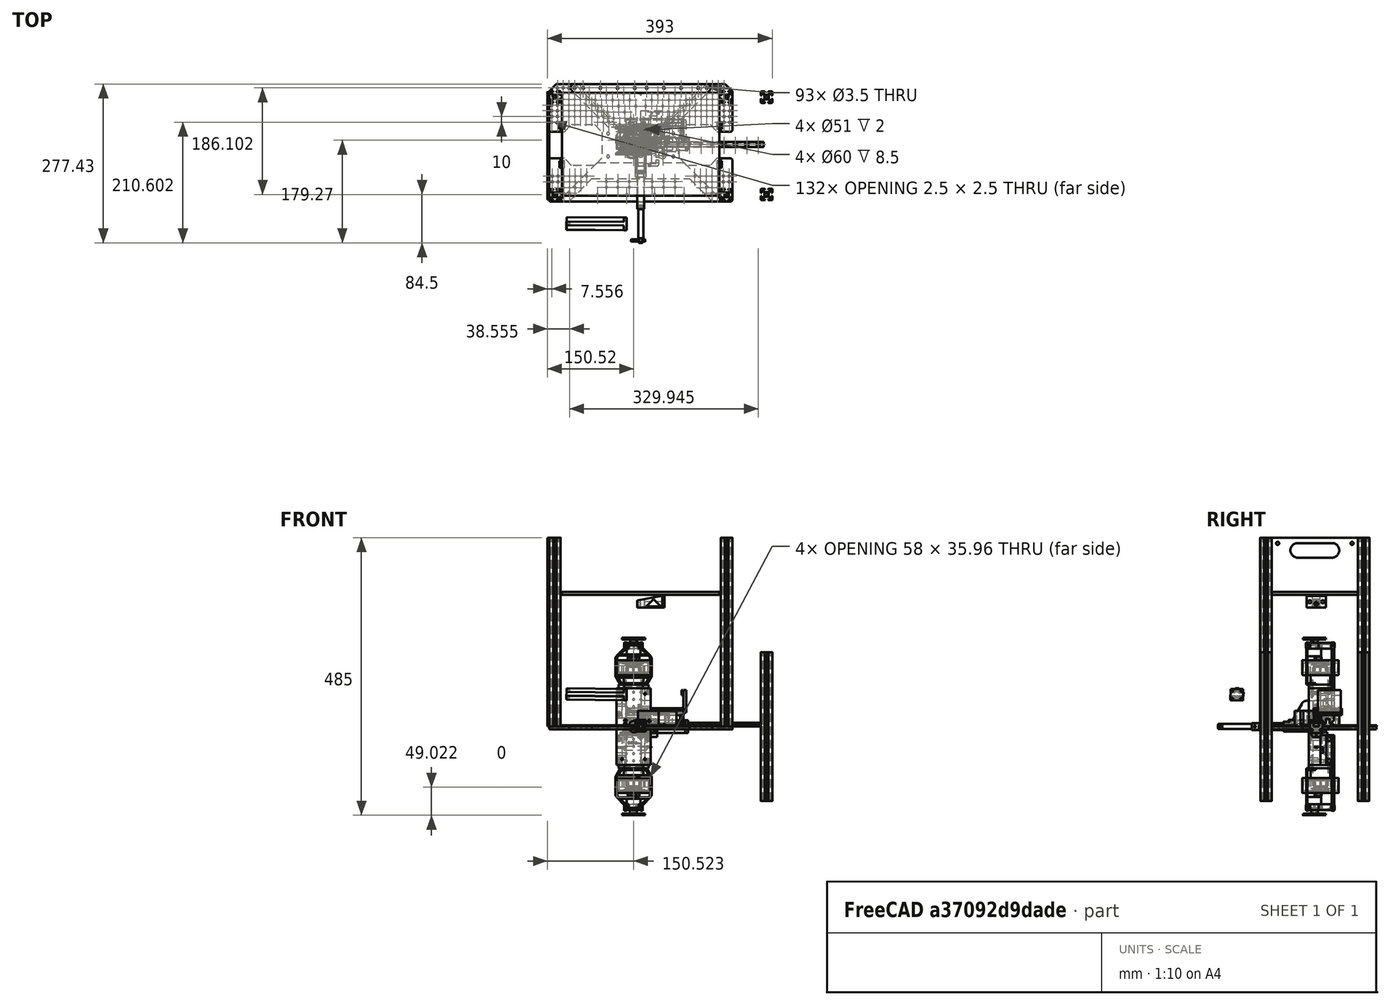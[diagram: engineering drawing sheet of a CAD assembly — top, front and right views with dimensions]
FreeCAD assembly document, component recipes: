
FREECAD ASSEMBLY — COMPONENT RECIPES ("NutSorter")

This assembly document has 31 components, labeled P0..P30 below (a component is one placed body or linked part). 29 of them carry a construction recipe — the FreeCAD feature program that regenerates the part from scratch, quoted from this document or its linked companion documents; the rest are supplied as boundary geometry only. No exploded tour is included for this assembly.
NOTE — document 2 of 2 of this assembly tour. The two overview renders and the header above are repeated from document 1; the component sections below continue where the previous document stopped.
COMPONENT P25 — recipe-attached ("Hiwin MGN9", modeled in this document).
Construction recipe (the document's own serialized feature program — sketch geometry with constraints, then the solid features built on it; lengths are millimeters unless a unit is written):

FEATURE [Sketcher::SketchObject] Sketch031
  ArcFitTolerance = 0
  AttachmentSupport = -> [YZ_Plane013]
  FullyConstrained = true
  MakeInternals = false
  MapMode = 5
  Placement = pos=(0,0,0) rot=(0.57735,0.57735,0.57735;2.0944rad)
  sketch-geometry (4):
    g0: LineSegment StartX=-4.5 StartY=0 StartZ=0 EndX=4.5 EndY=0 EndZ=0
    g1: LineSegment StartX=4.5 StartY=0 StartZ=0 EndX=4.5 EndY=6.5 EndZ=0
    g2: LineSegment StartX=4.5 StartY=6.5 StartZ=0 EndX=-4.5 EndY=6.5 EndZ=0
    g3: LineSegment StartX=-4.5 StartY=6.5 StartZ=0 EndX=-4.5 EndY=0 EndZ=0
  constraints (11):
    c: Coincident(g0,g1)
    c: Coincident(g1,g2)
    c: Coincident(g2,g3)
    c: Coincident(g3,g0)
    c: Horizontal(g0)
    c: Horizontal(g2)
    c: Vertical(g1)
    c: Vertical(g3)
    c: Symmetric(g0,g0,g-1)
    c: DistanceX(g0,g0) = 9  'width'
    c: DistanceY(g1,g1) = 6.5  'height'
FEATURE [PartDesign::Pad] Pad012
  Direction = (1,0,0)
  Length = 215
  Length2 = 10
  Placement = pos=(0,0,0) rot=(0.57735,0.57735,0.57735;2.0944rad)
  Profile = -> Sketch031
  ReferenceAxis = -> Sketch031 [N_Axis]
  Suppressed = false
  Type = 0
  expr: Length = Spreadsheet001.length
FEATURE [Sketcher::SketchObject] Sketch032
  ArcFitTolerance = 0
  AttachmentSupport = -> [YZ_Plane013]
  FullyConstrained = true
  MakeInternals = false
  MapMode = 5
  Placement = pos=(0,0,0) rot=(0.57735,-0.57735,-0.57735;2.0944rad)
  expr: Constraints[13] = 6.5 - 1.8
  expr: Constraints[14] = <<Sketch031>>.Constraints.width / 2 + 0.1 mm
  sketch-geometry (10):
    g0: ArcOfCircle CenterX=-4.6 CenterY=4.7 CenterZ=0 NormalX=0 NormalY=0 NormalZ=1 AngleXU=0 Radius=1 StartAngle=0.25268 EndAngle=6.03051
    g1: LineSegment StartX=-3.63175 StartY=4.95 StartZ=0 EndX=-3.13175 EndY=4.95 EndZ=0
    g2: LineSegment StartX=-3.13175 StartY=4.95 StartZ=0 EndX=-3.13175 EndY=4.45 EndZ=0
    g3: LineSegment StartX=-3.13175 StartY=4.45 StartZ=0 EndX=-3.63175 EndY=4.45 EndZ=0
    g4: LineSegment [constr] StartX=-4.6 StartY=4.7 StartZ=0 EndX=-3.13175 EndY=4.7 EndZ=0
    g5: ArcOfCircle CenterX=4.6 CenterY=4.7 CenterZ=0 NormalX=0 NormalY=0 NormalZ=1 AngleXU=0 Radius=1 StartAngle=3.39427 EndAngle=9.1721
    g6: LineSegment StartX=3.63175 StartY=4.95 StartZ=0 EndX=3.13175 EndY=4.95 EndZ=0
    g7: LineSegment StartX=3.13175 StartY=4.95 StartZ=0 EndX=3.13175 EndY=4.45 EndZ=0
    g8: LineSegment StartX=3.13175 StartY=4.45 StartZ=0 EndX=3.63175 EndY=4.45 EndZ=0
    g9: LineSegment [constr] StartX=4.6 StartY=4.7 StartZ=0 EndX=3.13175 EndY=4.7 EndZ=0
  constraints (29):
    c: Horizontal(g1)
    c: Coincident(g2,g1)
    c: Vertical(g2)
    c: Coincident(g3,g2)
    c: Horizontal(g3)
    c: Coincident(g4,g0)
    c: Horizontal(g4)
    c: Symmetric(g2,g1,g4)
    c: Coincident(g0,g3)
    c: Coincident(g0,g1)
    c: DistanceY(g2,g2) = 0.5
    c: DistanceX(g1,g1) = 0.5
    c: Diameter(g0) = 2
    c: DistanceY(g-1,g0) = 4.7
    c: DistanceX(g0,g-1) = 4.6
    c: Horizontal(g6)
    c: Coincident(g7,g6)
    c: Vertical(g7)
    c: Coincident(g8,g7)
    c: Horizontal(g8)
    c: Coincident(g9,g5)
    c: Horizontal(g9)
    c: Symmetric(g7,g6,g9)
    c: Coincident(g5,g8)
    c: Coincident(g5,g6)
    c: Diameter(g5) = 2
    c: Symmetric(g4,g9,g-2)
    c: Equal(g2,g7)
    c: Equal(g1,g6)
FEATURE [PartDesign::Pocket] Pocket015  label="Balls cut"
  BaseFeature = -> Pad012
  Direction = (1,0,0)
  Length = 5
  Length2 = 5
  Placement = pos=(0,0,0) rot=(0.57735,0.57735,0.57735;2.0944rad)
  Profile = -> Sketch032
  ReferenceAxis = -> Sketch032 [N_Axis]
  Suppressed = false
  Type = 1
FEATURE [Sketcher::SketchObject] Sketch033
  ArcFitTolerance = 0
  AttachmentOffset = pos=(5.5,0,0) rot=(0,0,1;1.5708rad)
  AttachmentSupport = -> [XY_Plane013]
  FullyConstrained = true
  MakeInternals = false
  MapMode = 5
  Placement = pos=(5.5,0,0) rot=(0,0,1;1.5708rad)
  expr: .AttachmentOffset.Base.x = Spreadsheet001.offset
  sketch-geometry (1):
    g0: Circle CenterX=0 CenterY=0 CenterZ=0 NormalX=0 NormalY=0 NormalZ=1 AngleXU=0 Radius=1.75
  constraints (2):
    c: Coincident(g0,g-1)
    c: Diameter(g0) = 3.5
FEATURE [PartDesign::Pocket] Pocket016  label="Screw hole"
  BaseFeature = -> Pocket015
  Direction = (0,0,-1)
  Length = 5
  Length2 = 5
  Midplane = true
  Placement = pos=(0,0,0) rot=(0.57735,0.57735,0.57735;2.0944rad)
  Profile = -> Sketch033
  ReferenceAxis = -> Sketch033 [N_Axis]
  Suppressed = false
  Type = 1
FEATURE [Sketcher::SketchObject] Sketch034
  ArcFitTolerance = 0
  AttachmentOffset = pos=(5.5,0,6.5) rot=(0,0,1;1.5708rad)
  AttachmentSupport = -> [XY_Plane013]
  FullyConstrained = true
  MakeInternals = false
  MapMode = 5
  Placement = pos=(5.5,0,6.5) rot=(0,0,1;1.5708rad)
  expr: .AttachmentOffset.Base.x = Spreadsheet001.offset
  expr: .AttachmentOffset.Base.z = Sketch031.Constraints.height
  sketch-geometry (1):
    g0: Circle CenterX=0 CenterY=0 CenterZ=0 NormalX=0 NormalY=0 NormalZ=1 AngleXU=0 Radius=3
  constraints (2):
    c: Coincident(g0,g-1)
    c: Diameter(g0) = 6
FEATURE [PartDesign::Pocket] Pocket017  label="Screw head cut"
  BaseFeature = -> Pocket016
  Direction = (0,0,-1)
  Length = 3.5
  Length2 = 5
  Placement = pos=(0,0,0) rot=(0.57735,0.57735,0.57735;2.0944rad)
  Profile = -> Sketch034
  ReferenceAxis = -> Sketch034 [N_Axis]
  Suppressed = false
  Type = 0
FEATURE [PartDesign::Chamfer] Chamfer001  label="Chamfer"
  Angle = 45
  Base = -> Pocket017 [Edge47]
  BaseFeature = -> Pocket017
  ChamferType = 0
  FlipDirection = false
  Placement = pos=(0,0,0) rot=(0.57735,0.57735,0.57735;2.0944rad)
  Size = 0.2
  Size2 = 1
  SupportTransform = false
  Suppressed = false
  UseAllEdges = false
FEATURE [PartDesign::LinearPattern] LinearPattern001  label="LinearPattern"
  BaseFeature = -> Chamfer001
  Direction = -> Sketch033 [V_Axis]
  Length = 200
  Mode = 0
  Occurrences = 11
  Offset = 20
  Originals = -> [Pocket016,Pocket017,Chamfer001]
  Placement = pos=(0,0,0) rot=(0.57735,0.57735,0.57735;2.0944rad)
  Reversed = true
  Suppressed = false
  TransformMode = 0
  expr: Length = Spreadsheet001.distance
  expr: Occurrences = Spreadsheet001.holes_number
FEATURE [PartDesign::Body] Body011  label="Hiwin rail MGN9R"
  AllowCompound = false
  Group = -> [Sketch031,Pad012,Sketch032,Pocket015,Sketch033,Pocket016,Sketch034,Pocket017,Chamfer001,LinearPattern001]
  Origin = -> Origin013
  Tip = -> LinearPattern001
COMPONENT P26 — geometry summary ("Partie mobile_Z"; no construction recipe available for this part):
  bounding box: 87.0 x 46.3 x 29.0 mm
  tessellated surface: 27,894 triangles
  volume: 28165 mm^3 (24% of its bounding box)
COMPONENT P27 — recipe-attached ("servo_DS3218MG003", modeled in this document).
Construction recipe (the document's own serialized feature program — sketch geometry with constraints, then the solid features built on it; lengths are millimeters unless a unit is written):

FEATURE [Sketcher::SketchObject] Sketch260
  ArcFitTolerance = 0
  AttachmentSupport = -> [XZ_Plane288]
  FullyConstrained = true
  MakeInternals = false
  MapMode = 5
  Placement = pos=(0,0,0) rot=(1,0,0;1.5708rad)
  expr: Constraints[19] = 19.8 / 2
  sketch-geometry (8):
    g0: LineSegment StartX=2.5 StartY=3.4 StartZ=0 EndX=2.5 EndY=0 EndZ=0
    g1: LineSegment StartX=2.5 StartY=0 StartZ=0 EndX=4.2 EndY=0 EndZ=0
    g2: LineSegment StartX=4.2 StartY=0 StartZ=0 EndX=4.2 EndY=2 EndZ=0
    g3: LineSegment StartX=4.2 StartY=2 StartZ=0 EndX=9.9 EndY=2 EndZ=0
    g4: LineSegment StartX=9.9 StartY=2 StartZ=0 EndX=9.9 EndY=4.4 EndZ=0
    g5: LineSegment StartX=9.9 StartY=4.4 StartZ=0 EndX=1.5 EndY=4.4 EndZ=0
    g6: LineSegment StartX=1.5 StartY=4.4 StartZ=0 EndX=1.5 EndY=3.4 EndZ=0
    g7: LineSegment StartX=1.5 StartY=3.4 StartZ=0 EndX=2.5 EndY=3.4 EndZ=0
  constraints (24):
    c: PointOnObject(g0,g-1)
    c: Vertical(g0)
    c: Coincident(g1,g0)
    c: PointOnObject(g1,g-1)
    c: Coincident(g2,g1)
    c: Vertical(g2)
    c: Coincident(g3,g2)
    c: Horizontal(g3)
    c: Coincident(g4,g3)
    c: Vertical(g4)
    c: Coincident(g5,g4)
    c: Horizontal(g5)
    c: Coincident(g6,g5)
    c: Coincident(g7,g6)
    c: Coincident(g7,g0)
    c: Horizontal(g7)
    c: Vertical(g6)
    c: DistanceY(g4,g4) = 2.4
    c: DistanceY(g2,g2) = 2
    c: DistanceX(g-1,g4) = 9.9
    c: DistanceX(g-1,g6) = 1.5
    c: DistanceY(g0,g0) = 3.4
    c: DistanceX(g-1,g0) = 2.5
    c: DistanceX(g1,g1) = 1.7
FEATURE [PartDesign::Revolution] Revolution002
  Angle = 360
  Angle2 = 60
  Axis = (0,2e-16,1)
  Base = (0,0,0)
  Placement = pos=(0,0,0) rot=(1,0,0;1.5708rad)
  Profile = -> Sketch260
  ReferenceAxis = -> Sketch260 [V_Axis]
  Reversed = true
  Suppressed = false
  Type = 0
FEATURE [Sketcher::SketchObject] Sketch261
  ArcFitTolerance = 0
  AttachmentSupport = -> [XY_Plane288]
  FullyConstrained = true
  MakeInternals = false
  MapMode = 5
  sketch-geometry (1):
    g0: Circle CenterX=-7 CenterY=0 CenterZ=0 NormalX=0 NormalY=0 NormalZ=1 AngleXU=0 Radius=1.2
  constraints (3):
    c: PointOnObject(g0,g-1)
    c: Diameter(g0) = 2.4
    c: DistanceX(g0,g-1) = 7
FEATURE [PartDesign::Pocket] Pocket111
  BaseFeature = -> Revolution002
  Direction = (0,0,-1)
  Length = 5
  Length2 = 5
  Midplane = true
  Placement = pos=(0,0,0) rot=(1,0,0;1.5708rad)
  Profile = -> Sketch261
  ReferenceAxis = -> Sketch261 [N_Axis]
  Suppressed = false
  Type = 1
FEATURE [PartDesign::PolarPattern] PolarPattern006
  Angle = 360
  Axis = -> Sketch261 [N_Axis]
  BaseFeature = -> Pocket111
  Mode = 0
  Occurrences = 4
  Offset = 120
  Originals = -> [Pocket111]
  Placement = pos=(0,0,0) rot=(1,0,0;1.5708rad)
  Suppressed = false
  TransformMode = 0
FEATURE [PartDesign::Body] Body010  label="Corps002"
  AllowCompound = false
  Group = -> [Sketch260,Revolution002,Sketch261,Pocket111,PolarPattern006]
  Origin = -> Origin291
  Placement = pos=(0,0,0.4) rot=(0,0,1;0rad)
  Tip = -> PolarPattern006
COMPONENT P28 — recipe-attached ("servo_DS3218MG005", modeled in this document).
Construction recipe (the document's own serialized feature program — sketch geometry with constraints, then the solid features built on it; lengths are millimeters unless a unit is written):

FEATURE [Sketcher::SketchObject] Sketch297
  ArcFitTolerance = 0
  AttachmentSupport = -> [XZ_Plane376]
  FullyConstrained = true
  MakeInternals = false
  MapMode = 5
  Placement = pos=(0,0,0) rot=(1,0,0;1.5708rad)
  expr: Constraints[19] = 19.8 / 2
  sketch-geometry (8):
    g0: LineSegment StartX=2.5 StartY=3.4 StartZ=0 EndX=2.5 EndY=0 EndZ=0
    g1: LineSegment StartX=2.5 StartY=0 StartZ=0 EndX=4.2 EndY=0 EndZ=0
    g2: LineSegment StartX=4.2 StartY=0 StartZ=0 EndX=4.2 EndY=2 EndZ=0
    g3: LineSegment StartX=4.2 StartY=2 StartZ=0 EndX=9.9 EndY=2 EndZ=0
    g4: LineSegment StartX=9.9 StartY=2 StartZ=0 EndX=9.9 EndY=4.4 EndZ=0
    g5: LineSegment StartX=9.9 StartY=4.4 StartZ=0 EndX=1.5 EndY=4.4 EndZ=0
    g6: LineSegment StartX=1.5 StartY=4.4 StartZ=0 EndX=1.5 EndY=3.4 EndZ=0
    g7: LineSegment StartX=1.5 StartY=3.4 StartZ=0 EndX=2.5 EndY=3.4 EndZ=0
  constraints (24):
    c: PointOnObject(g0,g-1)
    c: Vertical(g0)
    c: Coincident(g1,g0)
    c: PointOnObject(g1,g-1)
    c: Coincident(g2,g1)
    c: Vertical(g2)
    c: Coincident(g3,g2)
    c: Horizontal(g3)
    c: Coincident(g4,g3)
    c: Vertical(g4)
    c: Coincident(g5,g4)
    c: Horizontal(g5)
    c: Coincident(g6,g5)
    c: Coincident(g7,g6)
    c: Coincident(g7,g0)
    c: Horizontal(g7)
    c: Vertical(g6)
    c: DistanceY(g4,g4) = 2.4
    c: DistanceY(g2,g2) = 2
    c: DistanceX(g-1,g4) = 9.9
    c: DistanceX(g-1,g6) = 1.5
    c: DistanceY(g0,g0) = 3.4
    c: DistanceX(g-1,g0) = 2.5
    c: DistanceX(g1,g1) = 1.7
FEATURE [PartDesign::Revolution] Revolution003
  Angle = 360
  Angle2 = 60
  Axis = (0,2e-16,1)
  Base = (0,0,0)
  Placement = pos=(0,0,0) rot=(1,0,0;1.5708rad)
  Profile = -> Sketch297
  ReferenceAxis = -> Sketch297 [V_Axis]
  Reversed = true
  Suppressed = false
  Type = 0
FEATURE [Sketcher::SketchObject] Sketch298
  ArcFitTolerance = 0
  AttachmentSupport = -> [XY_Plane376]
  FullyConstrained = true
  MakeInternals = false
  MapMode = 5
  sketch-geometry (1):
    g0: Circle CenterX=-7 CenterY=0 CenterZ=0 NormalX=0 NormalY=0 NormalZ=1 AngleXU=0 Radius=1.2
  constraints (3):
    c: PointOnObject(g0,g-1)
    c: Diameter(g0) = 2.4
    c: DistanceX(g0,g-1) = 7
FEATURE [PartDesign::Pocket] Pocket129
  BaseFeature = -> Revolution003
  Direction = (0,0,-1)
  Length = 5
  Length2 = 5
  Midplane = true
  Placement = pos=(0,0,0) rot=(1,0,0;1.5708rad)
  Profile = -> Sketch298
  ReferenceAxis = -> Sketch298 [N_Axis]
  Suppressed = false
  Type = 1
FEATURE [PartDesign::PolarPattern] PolarPattern007
  Angle = 360
  Axis = -> Sketch298 [N_Axis]
  BaseFeature = -> Pocket129
  Mode = 0
  Occurrences = 4
  Offset = 120
  Originals = -> [Pocket129]
  Placement = pos=(0,0,0) rot=(1,0,0;1.5708rad)
  Suppressed = false
  TransformMode = 0
FEATURE [PartDesign::Body] Body098  label="Corps005"
  AllowCompound = false
  Group = -> [Sketch297,Revolution003,Sketch298,Pocket129,PolarPattern007]
  Origin = -> Origin379
  Placement = pos=(0,0,0.4) rot=(0,0,1;0rad)
  Tip = -> PolarPattern007
COMPONENT P29 — recipe-attached ("bras_002", modeled in this document).
Construction recipe (the document's own serialized feature program — sketch geometry with constraints, then the solid features built on it; lengths are millimeters unless a unit is written):

FEATURE [Sketcher::SketchObject] Sketch269
  ArcFitTolerance = 1e-06
  AttachmentSupport = -> [XY_Plane]
  FullyConstrained = true
  MakeInternals = false
  MapMode = 5
  expr: Constraints[18] = 14 / 2
  sketch-geometry (12):
    g0: ArcOfCircle CenterX=0 CenterY=0 CenterZ=0 NormalX=0 NormalY=0 NormalZ=1 AngleXU=0 Radius=10 StartAngle=1.5708 EndAngle=4.71239
    g1: ArcOfCircle CenterX=85 CenterY=5e-16 CenterZ=0 NormalX=0 NormalY=0 NormalZ=1 AngleXU=0 Radius=10 StartAngle=4.71239 EndAngle=7.85398
    g2: LineSegment StartX=-1.6e-15 StartY=10 StartZ=0 EndX=85 EndY=10 EndZ=0
    g3: LineSegment StartX=-1.8e-15 StartY=-10 StartZ=0 EndX=85 EndY=-10 EndZ=0
    g4: Circle CenterX=85 CenterY=5e-16 CenterZ=0 NormalX=0 NormalY=0 NormalZ=1 AngleXU=0 Radius=4
    g5: Circle CenterX=0 CenterY=7 CenterZ=0 NormalX=0 NormalY=0 NormalZ=1 AngleXU=0 Radius=1.5
    g6: Circle CenterX=7 CenterY=0 CenterZ=0 NormalX=0 NormalY=0 NormalZ=1 AngleXU=0 Radius=1.5
    g7: Circle CenterX=-7 CenterY=0 CenterZ=0 NormalX=0 NormalY=0 NormalZ=1 AngleXU=0 Radius=1.5
    g8: Circle CenterX=0 CenterY=-7 CenterZ=0 NormalX=0 NormalY=0 NormalZ=1 AngleXU=0 Radius=1.5
    g9: LineSegment [constr] StartX=0 StartY=7 StartZ=0 EndX=0 EndY=0 EndZ=0
    g10: LineSegment [constr] StartX=0 StartY=0 StartZ=0 EndX=7 EndY=0 EndZ=0
    g11: Circle CenterX=0 CenterY=0 CenterZ=0 NormalX=0 NormalY=0 NormalZ=1 AngleXU=0 Radius=2
  constraints (28):
    c: Tangent(g0,g2) = 1.5708
    c: Tangent(g0,g3) = -1.5708
    c: Tangent(g1,g2) = 1.5708
    c: Tangent(g1,g3) = -1.5708
    c: Equal(g0,g1)
    c: Horizontal(g3)
    c: Coincident(g4,g1)
    c: Diameter(g1) = 20
    c: PointOnObject(g5,g-2)
    c: PointOnObject(g6,g-1)
    c: PointOnObject(g7,g-1)
    c: PointOnObject(g8,g-2)
    c: Symmetric(g6,g7,g0)
    c: Symmetric(g5,g8,g0)
    c: Equal(g5,g7)
    c: Equal(g7,g8)
    c: Equal(g8,g6)
    c: Diameter(g5) = 3  'd_vis'
    c: DistanceY(g0,g5) = 7
    c: Coincident(g9,g5)
    c: Coincident(g9,g0)
    c: Coincident(g10,g0)
    c: Coincident(g10,g6)
    c: Equal(g10,g9)
    c: DistanceX(g0,g1) = 85
    c: Diameter(g4) = 8
    c: Coincident(g11,g0)
    c: Diameter(g11) = 4
FEATURE [PartDesign::Pad] Pad
  Direction = (0,0,1)
  Length = 4
  Length2 = 10
  Profile = -> Sketch269
  ReferenceAxis = -> Sketch269 [N_Axis]
  Suppressed = false
  Type = 0
FEATURE [PartDesign::Body] Body  label="bras_1"
  AllowCompound = false
  Group = -> [Sketch269,Pad]
  Origin = -> Origin
  Tip = -> Pad
COMPONENT P30 — recipe-attached ("servo_DS3218MG004", modeled in this document).
Construction recipe (the document's own serialized feature program — sketch geometry with constraints, then the solid features built on it; lengths are millimeters unless a unit is written):

FEATURE [Sketcher::SketchObject] Sketch048
  ArcFitTolerance = 0
  AttachmentSupport = -> [XZ_Plane021]
  FullyConstrained = true
  MakeInternals = false
  MapMode = 5
  Placement = pos=(0,0,0) rot=(1,0,0;1.5708rad)
  expr: Constraints[19] = 19.8 / 2
  sketch-geometry (8):
    g0: LineSegment StartX=2.5 StartY=3.4 StartZ=0 EndX=2.5 EndY=0 EndZ=0
    g1: LineSegment StartX=2.5 StartY=0 StartZ=0 EndX=4.2 EndY=0 EndZ=0
    g2: LineSegment StartX=4.2 StartY=0 StartZ=0 EndX=4.2 EndY=2 EndZ=0
    g3: LineSegment StartX=4.2 StartY=2 StartZ=0 EndX=9.9 EndY=2 EndZ=0
    g4: LineSegment StartX=9.9 StartY=2 StartZ=0 EndX=9.9 EndY=4.4 EndZ=0
    g5: LineSegment StartX=9.9 StartY=4.4 StartZ=0 EndX=1.5 EndY=4.4 EndZ=0
    g6: LineSegment StartX=1.5 StartY=4.4 StartZ=0 EndX=1.5 EndY=3.4 EndZ=0
    g7: LineSegment StartX=1.5 StartY=3.4 StartZ=0 EndX=2.5 EndY=3.4 EndZ=0
  constraints (24):
    c: PointOnObject(g0,g-1)
    c: Vertical(g0)
    c: Coincident(g1,g0)
    c: PointOnObject(g1,g-1)
    c: Coincident(g2,g1)
    c: Vertical(g2)
    c: Coincident(g3,g2)
    c: Horizontal(g3)
    c: Coincident(g4,g3)
    c: Vertical(g4)
    c: Coincident(g5,g4)
    c: Horizontal(g5)
    c: Coincident(g6,g5)
    c: Coincident(g7,g6)
    c: Coincident(g7,g0)
    c: Horizontal(g7)
    c: Vertical(g6)
    c: DistanceY(g4,g4) = 2.4
    c: DistanceY(g2,g2) = 2
    c: DistanceX(g-1,g4) = 9.9
    c: DistanceX(g-1,g6) = 1.5
    c: DistanceY(g0,g0) = 3.4
    c: DistanceX(g-1,g0) = 2.5
    c: DistanceX(g1,g1) = 1.7
FEATURE [PartDesign::Revolution] Revolution001
  Angle = 360
  Angle2 = 60
  Axis = (0,2e-16,1)
  Base = (0,0,0)
  Placement = pos=(0,0,0) rot=(1,0,0;1.5708rad)
  Profile = -> Sketch048
  ReferenceAxis = -> Sketch048 [V_Axis]
  Reversed = true
  Suppressed = false
  Type = 0
FEATURE [Sketcher::SketchObject] Sketch049
  ArcFitTolerance = 0
  AttachmentSupport = -> [XY_Plane021]
  FullyConstrained = true
  MakeInternals = false
  MapMode = 5
  sketch-geometry (1):
    g0: Circle CenterX=-7 CenterY=0 CenterZ=0 NormalX=0 NormalY=0 NormalZ=1 AngleXU=0 Radius=1.2
  constraints (3):
    c: PointOnObject(g0,g-1)
    c: Diameter(g0) = 2.4
    c: DistanceX(g0,g-1) = 7
FEATURE [PartDesign::Pocket] Pocket025
  BaseFeature = -> Revolution001
  Direction = (0,0,-1)
  Length = 5
  Length2 = 5
  Midplane = true
  Placement = pos=(0,0,0) rot=(1,0,0;1.5708rad)
  Profile = -> Sketch049
  ReferenceAxis = -> Sketch049 [N_Axis]
  Suppressed = false
  Type = 1
FEATURE [PartDesign::PolarPattern] PolarPattern003
  Angle = 360
  Axis = -> Sketch049 [N_Axis]
  BaseFeature = -> Pocket025
  Mode = 0
  Occurrences = 4
  Offset = 120
  Originals = -> [Pocket025]
  Placement = pos=(0,0,0) rot=(1,0,0;1.5708rad)
  Suppressed = false
  TransformMode = 0
FEATURE [PartDesign::Body] Body014  label="Corps001"
  AllowCompound = false
  Group = -> [Sketch048,Revolution001,Sketch049,Pocket025,PolarPattern003]
  Origin = -> Origin021
  Placement = pos=(0,0,0.4) rot=(0,0,1;0rad)
  Tip = -> PolarPattern003
PROVENANCE & LICENSES
A FreeCAD (.FCStd) document from a public repository crawl; recipes are the document's own serialized feature recipes (and, for linked parts, companion documents' recipes).
License: as declared in the source repository (recorded in the dataset sidecar).
